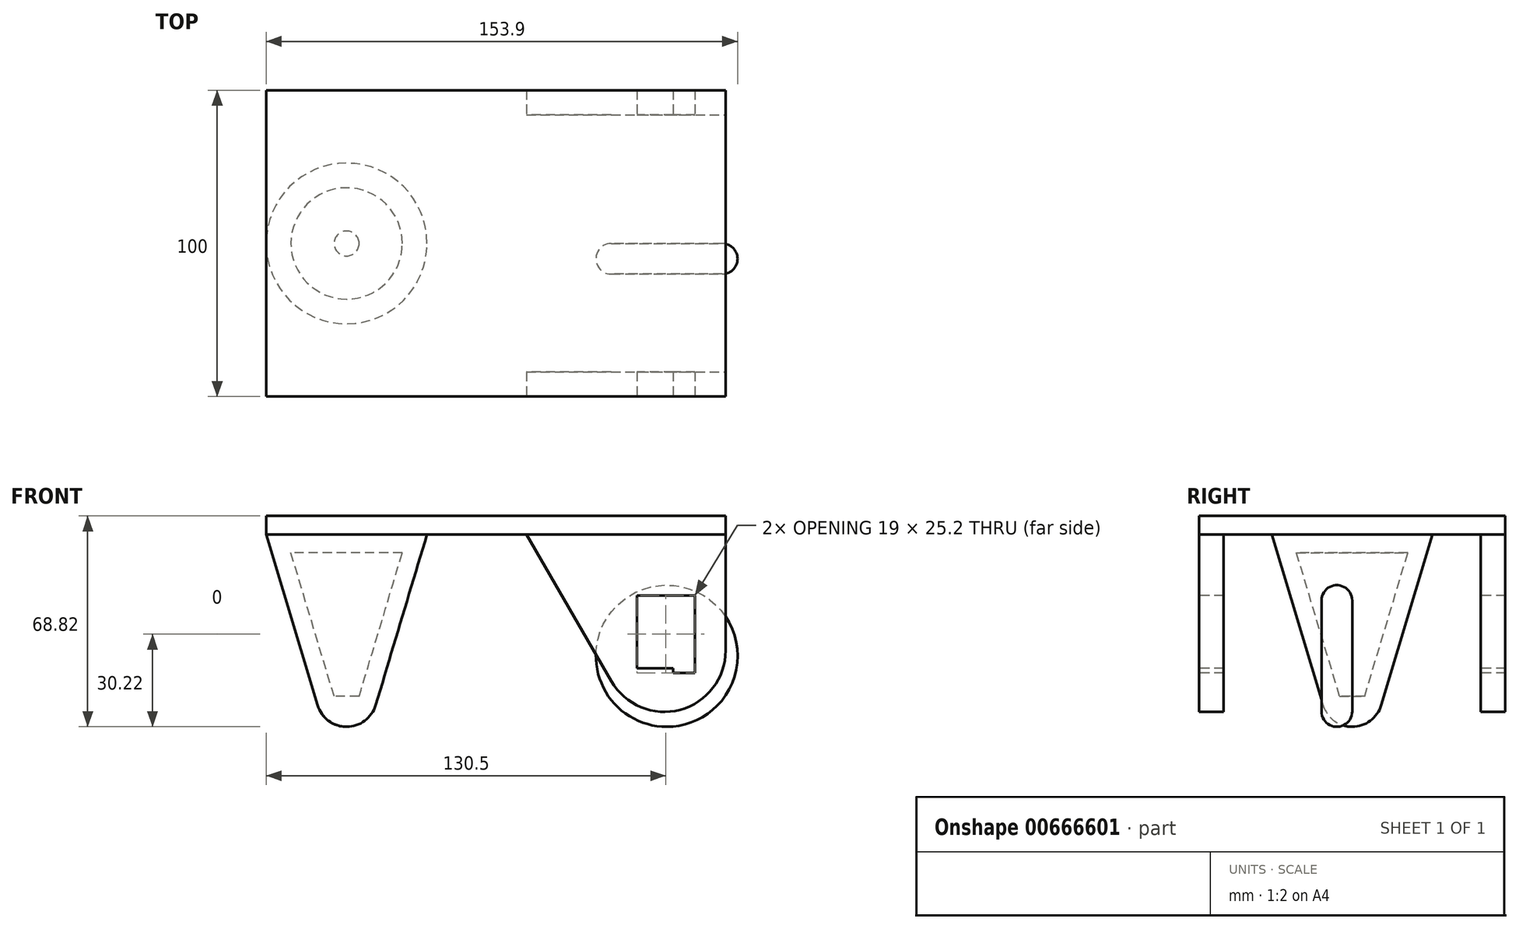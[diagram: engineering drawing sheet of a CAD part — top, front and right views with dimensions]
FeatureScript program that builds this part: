
annotation { "Feature Type Name" : "Feature", "Feature Type Description" : "" }
export const myFeature = defineFeature(function(context is Context, id is Id, definition is map)
    precondition{}
    {
        {
            var Q0;
            Q0=qCreatedBy(makeId("Top.planeOp"),FACE);
            var sketch = newSketch(context, id + "F0", { "sketchPlane" : qUnion([Q0])});
            skLineSegment(sketch, "E0.bottom", {"start": v(-75, 50) * mm, "end": v(75, 50) * mm});
            skLineSegment(sketch, "E0.top", {"start": v(-75, -50) * mm, "end": v(75, -50) * mm});
            skLineSegment(sketch, "E0.left", {"start": v(-75, 50) * mm, "end": v(-75, -50) * mm});
            skLineSegment(sketch, "E0.right", {"start": v(75, 50) * mm, "end": v(75, -50) * mm});
            skPoint(sketch, "E0.middle", {"position": v(0, 0) * mm});
            skSolve(sketch);
        }
        {
            var Q0;
            Q0=makeQuery(id+"F0.imprint","IMPRINT",FACE,{"disambiguationData":[TD([[makeQuery(id+"F0.imprint","IMPRINT",EDGE,{"derivedFrom":sQuery(id+"F0.wireOp",EDGE,"E0.bottom")}),-1.0]])]});
            extrude(context, id + "F1", {"entities" : qUnion([Q0]), "depth" : 6 * mm, "offsetDistance" : 25.4 * mm});
        }
        {
            var Q0;
            Q0=makeQuery(id+"F1.opExtrude","SWEPT_FACE",FACE,{"disambiguationData":[OSD([sQuery(id+"F0.wireOp",EDGE,"E0.top")])]});
            var sketch = newSketch(context, id + "F2", { "sketchPlane" : qUnion([Q0])});
            skLineSegment(sketch, "E1", {"start": v(65, -20) * mm, "end": v(46, -20) * mm});
            skLineSegment(sketch, "E2", {"start": v(10, 0) * mm, "end": v(75, 0) * mm});
            skLineSegment(sketch, "E3", {"start": v(75, 0) * mm, "end": v(75, -37.94) * mm});
            skLineSegment(sketch, "E4", {"start": v(10, 0) * mm, "end": v(37.68, -47.94) * mm});
            skArc(sketch, "E5.filletArc", {"start": v(37.68, -47.94) * mm, "mid": v(60.18, -57.26) * mm, "end": v(75, -37.94) * mm});
            skLineSegment(sketch, "E6.MirrorCS", {"start": v(57.8, -43.7) * mm, "end": v(57.8, -45.2) * mm});
            skLineSegment(sketch, "E7.MirrorCS", {"start": v(46, -43.7) * mm, "end": v(57.8, -43.7) * mm});
            skLineSegment(sketch, "E8.MirrorCS", {"start": v(46, -43.7) * mm, "end": v(46, -20) * mm});
            skLineSegment(sketch, "E9.MirrorCS", {"start": v(65, -45.2) * mm, "end": v(65, -20) * mm});
            skLineSegment(sketch, "E10.MirrorCS", {"start": v(57.8, -45.2) * mm, "end": v(65, -45.2) * mm});
            skSolve(sketch);
        }
        {
            var Q0;
            Q0=qCreatedBy(makeId("Top.planeOp"),FACE);
            var sketch = newSketch(context, id + "F3", { "sketchPlane" : qUnion([Q0])});
            skLineSegment(sketch, "E11.bottom", {"start": v(-60.46, 42) * mm, "end": v(110.6, 42) * mm});
            skLineSegment(sketch, "E11.top", {"start": v(-60.46, -42) * mm, "end": v(110.6, -42) * mm});
            skLineSegment(sketch, "E11.left", {"start": v(-60.46, 42) * mm, "end": v(-60.46, -42) * mm});
            skLineSegment(sketch, "E11.right", {"start": v(110.6, 42) * mm, "end": v(110.6, -42) * mm});
            skSolve(sketch);
        }
        {
            var Q0;
            Q0=qCreatedBy(makeId("Front.planeOp"),FACE);
            var sketch = newSketch(context, id + "F4", { "sketchPlane" : qUnion([Q0])});
            skLineSegment(sketch, "E12", {"start": v(-75, 0) * mm, "end": v(-48.74, 0) * mm});
            skLineSegment(sketch, "E13", {"start": v(-48.74, 0) * mm, "end": v(-48.74, -87.3) * mm});
            skLineSegment(sketch, "E14", {"start": v(-48.74, -87.3) * mm, "end": v(-75, 0) * mm});
            skCircle(sketch, "E15", {"center": v(-48.74, -52.92) * mm, "radius": 9.9 * mm});
            skLineSegment(sketch, "E16", {"start": v(-48.74, -6) * mm, "end": v(-66.93, -6) * mm});
            skLineSegment(sketch, "E17", {"start": v(-66.93, -6) * mm, "end": v(-52.82, -52.92) * mm});
            skLineSegment(sketch, "E18", {"start": v(-52.82, -52.92) * mm, "end": v(-48.74, -52.92) * mm});
            skLineSegment(sketch, "E19", {"start": v(-48.74, -62.82) * mm, "end": v(75.33, -62.82) * mm});
            skCircle(sketch, "E20", {"center": v(55.77, -39.7) * mm, "radius": 23.12 * mm});
            skSolve(sketch);
        }
        {
            var Q0;
            Q0=makeQuery(id+"F2.imprint","IMPRINT",FACE,{"disambiguationData":[TD([[makeQuery(id+"F2.imprint","IMPRINT",EDGE,{"derivedFrom":sQuery(id+"F2.wireOp",EDGE,"E1")}),-1.0]])]});
            extrude(context, id + "F5", {"entities" : qUnion([Q0]), "oppositeDirection" : true, "depth" : 100 * mm, "offsetDistance" : 25 * mm});
        }
        {
            var Q0;
            Q0=makeQuery(id+"F3.imprint","IMPRINT",FACE,{"disambiguationData":[TD([[makeQuery(id+"F3.imprint","IMPRINT",EDGE,{"derivedFrom":sQuery(id+"F3.wireOp",EDGE,"E11.bottom")}),-1.0]])]});
            extrude(context, id + "F6", {"entities" : qUnion([Q0]), "operationType" : NewBodyOperationType.REMOVE, "oppositeDirection" : true, "depth" : 200 * mm, "offsetDistance" : 25 * mm});
        }
        {
            var Q0;
            {var subQ5=sQuery(id+"F4.wireOp",EDGE,"E12");Q0=makeQuery(id+"F4.imprint","IMPRINT",FACE,{"disambiguationData":[TD([[makeQuery(id+"F4.imprint","IMPRINT",EDGE,{"derivedFrom":subQ5}),-1.0]])]});}
            var Q1;
            {var subQ4=sQuery(id+"F4.wireOp",EDGE,"E18");Q1=makeQuery(id+"F4.imprint","IMPRINT",FACE,{"disambiguationData":[TD([[makeQuery(id+"F4.imprint","IMPRINT",EDGE,{"derivedFrom":subQ4}),-1.0]])]});}
            var Q2;
            Q2=sQuery(id+"F4.wireOp",EDGE,"E13");
            revolve(context, id + "F7", {"operationType" : NewBodyOperationType.ADD, "entities" : qUnion([Q0, Q1]), "axis" : qUnion([Q2]), "revolveType" : RevolveType.FULL});
        }
        {
            var Q0;
            Q0=makeQuery(id+"F4.imprint","IMPRINT",FACE,{"disambiguationData":[TD([[makeQuery(id+"F4.imprint","IMPRINT",EDGE,{"derivedFrom":sQuery(id+"F4.wireOp",EDGE,"E20")}),1.0]])]});
            extrude(context, id + "F8", {"entities" : qUnion([Q0]), "depth" : 10 * mm, "offsetDistance" : 25 * mm});
        }
        {
            var Q0;
            Q0=makeQuery(id+"F8.opExtrude","SWEPT_FACE",FACE,{"disambiguationData":[OSD([sQuery(id+"F4.wireOp",EDGE,"E20")])]});
            fillet(context, id + "F9", {"entities" : qUnion([Q0]), "radius" : 5 * mm, "tangentPropagation" : true, "allowEdgeOverflow" : false});
        }
    });
